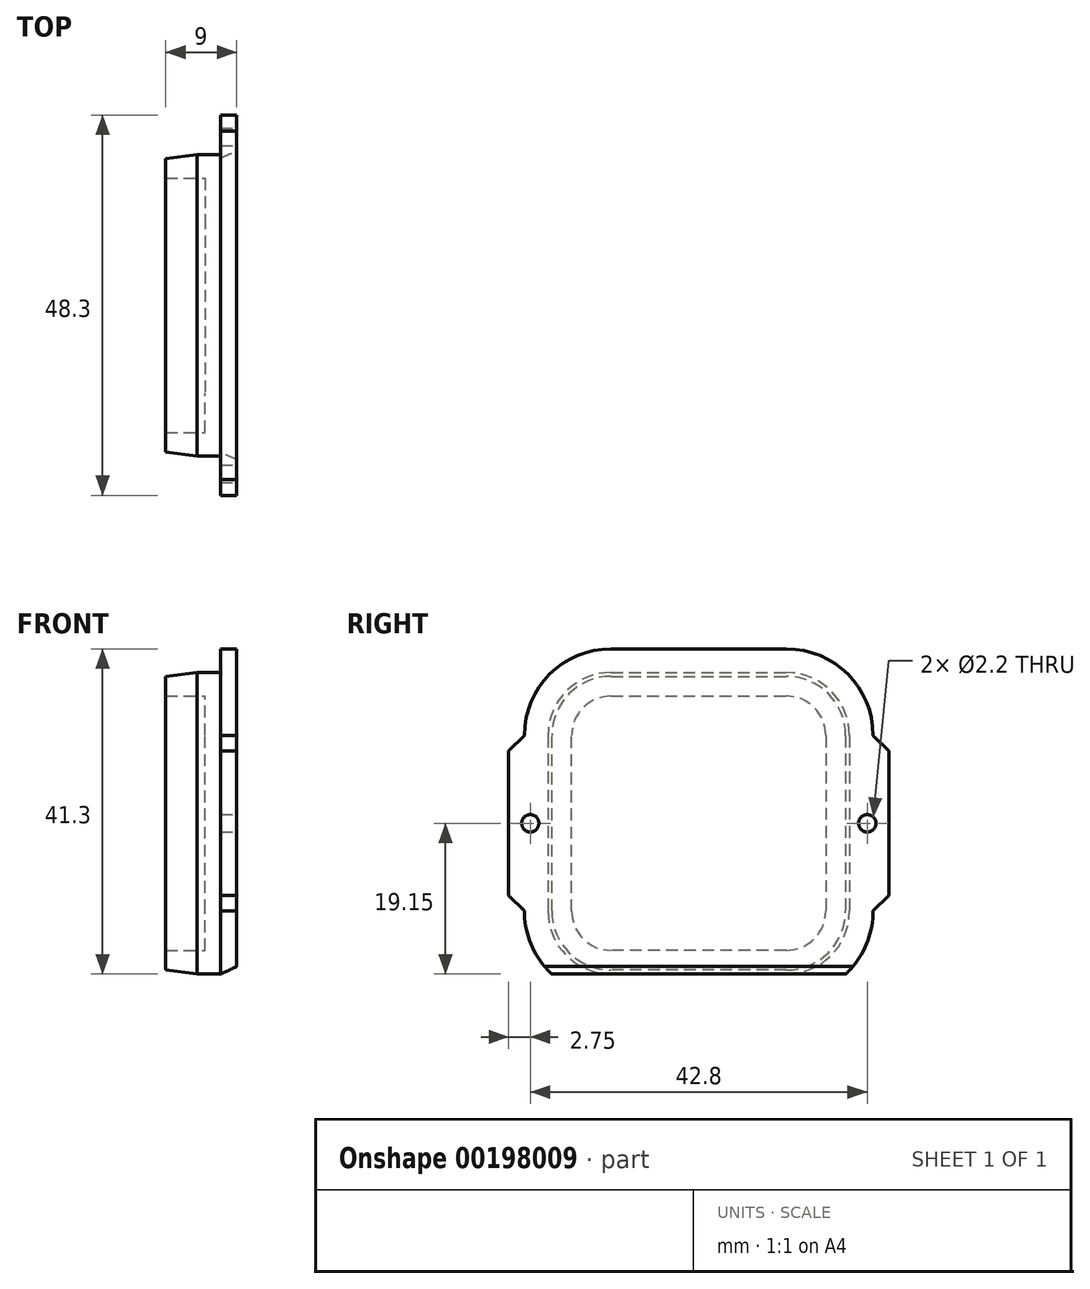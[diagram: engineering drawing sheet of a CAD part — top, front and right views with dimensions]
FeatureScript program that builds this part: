
annotation { "Feature Type Name" : "Feature", "Feature Type Description" : "" }
export const myFeature = defineFeature(function(context is Context, id is Id, definition is map)
    precondition{}
    {
        {
            var Q0;
            Q0=qCreatedBy(makeId("Right.planeOp"),FACE);
            var sketch = newSketch(context, id + "F0", { "sketchPlane" : qUnion([Q0])});
            skLineSegment(sketch, "E0.bottom", {"start": v(-11.15, 18.65) * mm, "end": v(11.15, 18.65) * mm});
            skLineSegment(sketch, "E0.top", {"start": v(-11.15, -19.65) * mm, "end": v(11.15, -19.65) * mm});
            skLineSegment(sketch, "E0.left", {"start": v(-19.15, 10.65) * mm, "end": v(-19.15, -11.65) * mm});
            skLineSegment(sketch, "E0.right", {"start": v(19.15, 10.65) * mm, "end": v(19.15, -11.65) * mm});
            skPoint(sketch, "E1.visualSharp", {"position": v(-19.15, 18.65) * mm});
            skArc(sketch, "E1.filletArc", {"start": v(-11.15, 18.65) * mm, "mid": v(-16.8, 16.3) * mm, "end": v(-19.15, 10.65) * mm});
            skPoint(sketch, "E2.visualSharp", {"position": v(19.15, 18.65) * mm});
            skArc(sketch, "E2.filletArc", {"start": v(19.15, 10.65) * mm, "mid": v(16.8, 16.3) * mm, "end": v(11.15, 18.65) * mm});
            skPoint(sketch, "E3.visualSharp", {"position": v(19.15, -19.65) * mm});
            skArc(sketch, "E3.filletArc", {"start": v(11.15, -19.65) * mm, "mid": v(16.8, -17.3) * mm, "end": v(19.15, -11.65) * mm});
            skPoint(sketch, "E4.visualSharp", {"position": v(-19.15, -19.65) * mm});
            skArc(sketch, "E4.filletArc", {"start": v(-19.15, -11.65) * mm, "mid": v(-16.8, -17.3) * mm, "end": v(-11.15, -19.65) * mm});
            skArc(sketch, "E5.0", {"start": v(-11.15, 21.65) * mm, "mid": v(-18.93, 18.43) * mm, "end": v(-22.15, 10.65) * mm});
            skLineSegment(sketch, "E5.1", {"start": v(-22.15, 10.65) * mm, "end": v(-22.15, -11.65) * mm});
            skLineSegment(sketch, "E5.2", {"start": v(-11.15, 21.65) * mm, "end": v(11.15, 21.65) * mm});
            skArc(sketch, "E5.3", {"start": v(-22.15, -11.65) * mm, "mid": v(-18.93, -19.43) * mm, "end": v(-11.15, -22.65) * mm});
            skArc(sketch, "E5.4", {"start": v(22.15, 10.65) * mm, "mid": v(18.93, 18.43) * mm, "end": v(11.15, 21.65) * mm});
            skLineSegment(sketch, "E5.5", {"start": v(22.15, 10.65) * mm, "end": v(22.15, -11.65) * mm});
            skArc(sketch, "E5.6", {"start": v(11.15, -22.65) * mm, "mid": v(18.93, -19.43) * mm, "end": v(22.15, -11.65) * mm});
            skLineSegment(sketch, "E5.7", {"start": v(-11.15, -22.65) * mm, "end": v(11.15, -22.65) * mm});
            skLineSegment(sketch, "E6", {"start": v(-24.15, -9.65) * mm, "end": v(-24.15, 8.65) * mm});
            skLineSegment(sketch, "E7", {"start": v(-24.15, 8.65) * mm, "end": v(-22.15, 10.65) * mm});
            skLineSegment(sketch, "E8", {"start": v(-22.15, -11.65) * mm, "end": v(-24.15, -9.65) * mm});
            skLineSegment(sketch, "E9.MirrorCS", {"start": v(24.15, 8.65) * mm, "end": v(22.15, 10.65) * mm});
            skLineSegment(sketch, "E10.MirrorCS", {"start": v(24.15, -9.65) * mm, "end": v(24.15, 8.65) * mm});
            skLineSegment(sketch, "E11.MirrorCS", {"start": v(22.15, -11.65) * mm, "end": v(24.15, -9.65) * mm});
            skLineSegment(sketch, "E12", {"start": v(-19.15, -0.5) * mm, "end": v(19.15, -0.5) * mm, "construction": true});
            skLineSegment(sketch, "E13", {"start": v(0, 18.65) * mm, "end": v(0, -19.65) * mm, "construction": true});
            skPoint(sketch, "E14.visualSharp", {"position": v(-16.65, 16.65) * mm});
            skPoint(sketch, "E15", {"position": v(-21.4, -0.5) * mm});
            skPoint(sketch, "E16", {"position": v(-22.15, -0.5) * mm});
            skPoint(sketch, "E17.MirrorP", {"position": v(21.4, -0.5) * mm});
            skSolve(sketch);
        }
        {
            var Q0;
            Q0=makeQuery(id+"F0.imprint","IMPRINT",FACE,{"disambiguationData":[TD([[makeQuery(id+"F0.imprint","IMPRINT",EDGE,{"derivedFrom":sQuery(id+"F0.wireOp",EDGE,"E0.bottom")}),-1.0]])]});
            var Q1;
            Q1=makeQuery(id+"F0.imprint","IMPRINT",FACE,{"disambiguationData":[TD([[makeQuery(id+"F0.imprint","IMPRINT",EDGE,{"derivedFrom":sQuery(id+"F0.wireOp",EDGE,"E0.bottom")}),1.0]])]});
            var Q2;
            Q2=makeQuery(id+"F0.imprint","IMPRINT",FACE,{"disambiguationData":[TD([[makeQuery(id+"F0.imprint","IMPRINT",EDGE,{"derivedFrom":sQuery(id+"F0.wireOp",EDGE,"E5.1")}),-1.0]])]});
            var Q3;
            Q3=makeQuery(id+"F0.imprint","IMPRINT",FACE,{"disambiguationData":[TD([[makeQuery(id+"F0.imprint","IMPRINT",EDGE,{"derivedFrom":sQuery(id+"F0.wireOp",EDGE,"E5.5")}),1.0]])]});
            extrude(context, id + "F1", {"entities" : qUnion([Q0, Q1, Q2, Q3]), "oppositeDirection" : true, "depth" : 2 * mm});
        }
        {
            var Q0;
            Q0=makeQuery(id+"F0.imprint","IMPRINT",FACE,{"disambiguationData":[TD([[makeQuery(id+"F0.imprint","IMPRINT",EDGE,{"derivedFrom":sQuery(id+"F0.wireOp",EDGE,"E0.bottom")}),-1.0]])]});
            extrude(context, id + "F2", {"entities" : qUnion([Q0]), "operationType" : NewBodyOperationType.ADD, "oppositeDirection" : true, "depth" : 4 * mm});
        }
        {
            var Q0;
            Q0=makeQuery(id+"F2.boolean.opBoolean","INTERSECT",EDGE,{"derivedFrom":[makeQuery(id+"F1.opExtrude","CAP_FACE",FACE,{"disambiguationData":[OSD([sQuery(id+"F0.wireOp",EDGE,"E5.0"),sQuery(id+"F0.wireOp",EDGE,"E5.2"),sQuery(id+"F0.wireOp",EDGE,"E5.3"),sQuery(id+"F0.wireOp",EDGE,"E5.4"),sQuery(id+"F0.wireOp",EDGE,"E5.6"),sQuery(id+"F0.wireOp",EDGE,"E5.7"),sQuery(id+"F0.wireOp",EDGE,"E6"),sQuery(id+"F0.wireOp",EDGE,"E7"),sQuery(id+"F0.wireOp",EDGE,"E8"),sQuery(id+"F0.wireOp",EDGE,"E9.MirrorCS"),sQuery(id+"F0.wireOp",EDGE,"E10.MirrorCS"),sQuery(id+"F0.wireOp",EDGE,"E11.MirrorCS"),sQuery(id+"F0.wireOp",EDGE,"RST1X7r3-oKxB-jdrm-FJc1-FZEFyPknjC7n.bottom"),sQuery(id+"F0.wireOp",EDGE,"RST1X7r3-oKxB-jdrm-FJc1-FZEFyPknjC7n.top"),sQuery(id+"F0.wireOp",EDGE,"RST1X7r3-oKxB-jdrm-FJc1-FZEFyPknjC7n.left"),sQuery(id+"F0.wireOp",EDGE,"RST1X7r3-oKxB-jdrm-FJc1-FZEFyPknjC7n.right"),sQuery(id+"F0.wireOp",EDGE,"f47886a1-abc6-43d7-98a8-f8cff71f392d.filletArc"),sQuery(id+"F0.wireOp",EDGE,"5e3ffb94-8ac9-4c8a-9269-9c21b55e64ff.filletArc"),sQuery(id+"F0.wireOp",EDGE,"dd1fbfdf-1fb2-4afd-85d2-cb31fff93166.filletArc"),sQuery(id+"F0.wireOp",EDGE,"E14.filletArc"),sQuery(id+"F0.wireOp",EDGE,"41707f4f-61de-468e-8cde-fad0d991ba2c0.MirrorCS"),sQuery(id+"F0.wireOp",EDGE,"c94bd9be-500d-4d44-b017-d16b26a63a020.MirrorCS"),sQuery(id+"F0.wireOp",EDGE,"8c78eab5-b810-45c1-9855-b0b5e582e1f70.MirrorCS"),sQuery(id+"F0.wireOp",EDGE,"6b2eb93e-fa95-4abc-8643-495f8d23bd850.MirrorCS"),sQuery(id+"F0.wireOp",EDGE,"e98be541-006e-4dad-bcde-d64d35c2e2500.MirrorCS"),sQuery(id+"F0.wireOp",EDGE,"3a2f4d0b-5016-42d9-9411-d42ab24a4ea80.MirrorCS"),sQuery(id+"F0.wireOp",EDGE,"9864ca3c-7186-4b8b-bf48-64fe2223f2a70.MirrorCS"),sQuery(id+"F0.wireOp",EDGE,"28ad38c3-9f67-4266-9024-0f2c2453c1940.MirrorCS"),sQuery(id+"F0.wireOp",EDGE,"bd4dbd89-46a3-4a25-ba81-fe0fc24358690.MirrorCS"),sQuery(id+"F0.wireOp",EDGE,"919fa4dc-a3d8-4998-9de8-7e6e011190fa0.MirrorCS"),sQuery(id+"F0.wireOp",EDGE,"c0e8c9a9-4d36-41b1-b5ef-4927e6b5828c0.MirrorCS"),sQuery(id+"F0.wireOp",EDGE,"65d96819-48be-4bb4-90a4-4548596de35d0.MirrorCS"),sQuery(id+"F0.wireOp",EDGE,"d78f8fef-45e7-4f36-8306-dc5005d627950.MirrorCS"),sQuery(id+"F0.wireOp",EDGE,"cc93ec59-fd94-4fdf-a76b-cf34ac5038500.MirrorCS"),sQuery(id+"F0.wireOp",EDGE,"b5ffeaaf-6a07-455a-ac6d-026a3d01b9ef0.MirrorCS"),sQuery(id+"F0.wireOp",EDGE,"54cb0ba3-91fc-40b9-bd3f-aec4dbbdf1710.MirrorCS"),sQuery(id+"F0.wireOp",EDGE,"ed805bfa-8f41-4e78-a241-45e0847f27010.MirrorCS"),sQuery(id+"F0.wireOp",EDGE,"2de16986-fcdf-4a11-be1b-2661225e98d80.MirrorCS"),sQuery(id+"F0.wireOp",EDGE,"56bdd509-48f3-4dbd-af82-ea80d3fc59200.MirrorCS"),sQuery(id+"F0.wireOp",EDGE,"176b7e12-560a-4aa1-b38f-03d71e9105200.MirrorCS"),sQuery(id+"F0.wireOp",EDGE,"0f632275-472d-4092-9a11-c3f5ca6ce4e90.MirrorCS"),sQuery(id+"F0.wireOp",EDGE,"313d3c47-0811-412c-b21b-6fa3ed4e9cd90.MirrorCS"),sQuery(id+"F0.wireOp",EDGE,"c9272683-ccd8-4751-98f5-67358050bd030.MirrorCS"),sQuery(id+"F0.wireOp",EDGE,"8fdea69b-69b8-45bc-b756-b638989ef7c50.MirrorCS")])],"isStart":false}),makeQuery(id+"F2.opExtrude","SWEPT_FACE",FACE,{"disambiguationData":[OSD([sQuery(id+"F0.wireOp",EDGE,"E0.top")])]})]});
            var Q1;
            {var subQ0=sQuery(id+"F0.wireOp",EDGE,"E14.filletArc");var subQ1=sQuery(id+"F0.wireOp",EDGE,"0f632275-472d-4092-9a11-c3f5ca6ce4e90.MirrorCS");var subQ2=sQuery(id+"F0.wireOp",EDGE,"d78f8fef-45e7-4f36-8306-dc5005d627950.MirrorCS");var subQ3=sQuery(id+"F0.wireOp",EDGE,"e98be541-006e-4dad-bcde-d64d35c2e2500.MirrorCS");Q1=makeQuery(id+"F9bfLVA2CBOZj6R_1.boolean.opBoolean","MERGE",FACE,{"derivedFrom":[makeQuery(id+"F1.opExtrude","CAP_FACE",FACE,{"disambiguationData":[OSD([sQuery(id+"F0.wireOp",EDGE,"E5.0"),sQuery(id+"F0.wireOp",EDGE,"E5.2"),sQuery(id+"F0.wireOp",EDGE,"E5.3"),sQuery(id+"F0.wireOp",EDGE,"E5.4"),sQuery(id+"F0.wireOp",EDGE,"E5.6"),sQuery(id+"F0.wireOp",EDGE,"E5.7"),sQuery(id+"F0.wireOp",EDGE,"E6"),sQuery(id+"F0.wireOp",EDGE,"E7"),sQuery(id+"F0.wireOp",EDGE,"E8"),sQuery(id+"F0.wireOp",EDGE,"E9.MirrorCS"),sQuery(id+"F0.wireOp",EDGE,"E10.MirrorCS"),sQuery(id+"F0.wireOp",EDGE,"E11.MirrorCS"),sQuery(id+"F0.wireOp",EDGE,"RST1X7r3-oKxB-jdrm-FJc1-FZEFyPknjC7n.bottom"),sQuery(id+"F0.wireOp",EDGE,"RST1X7r3-oKxB-jdrm-FJc1-FZEFyPknjC7n.top"),sQuery(id+"F0.wireOp",EDGE,"RST1X7r3-oKxB-jdrm-FJc1-FZEFyPknjC7n.left"),sQuery(id+"F0.wireOp",EDGE,"RST1X7r3-oKxB-jdrm-FJc1-FZEFyPknjC7n.right"),sQuery(id+"F0.wireOp",EDGE,"f47886a1-abc6-43d7-98a8-f8cff71f392d.filletArc"),sQuery(id+"F0.wireOp",EDGE,"5e3ffb94-8ac9-4c8a-9269-9c21b55e64ff.filletArc"),sQuery(id+"F0.wireOp",EDGE,"dd1fbfdf-1fb2-4afd-85d2-cb31fff93166.filletArc"),subQ0,sQuery(id+"F0.wireOp",EDGE,"41707f4f-61de-468e-8cde-fad0d991ba2c0.MirrorCS"),sQuery(id+"F0.wireOp",EDGE,"c94bd9be-500d-4d44-b017-d16b26a63a020.MirrorCS"),sQuery(id+"F0.wireOp",EDGE,"8c78eab5-b810-45c1-9855-b0b5e582e1f70.MirrorCS"),sQuery(id+"F0.wireOp",EDGE,"6b2eb93e-fa95-4abc-8643-495f8d23bd850.MirrorCS"),subQ3,sQuery(id+"F0.wireOp",EDGE,"3a2f4d0b-5016-42d9-9411-d42ab24a4ea80.MirrorCS"),sQuery(id+"F0.wireOp",EDGE,"9864ca3c-7186-4b8b-bf48-64fe2223f2a70.MirrorCS"),sQuery(id+"F0.wireOp",EDGE,"28ad38c3-9f67-4266-9024-0f2c2453c1940.MirrorCS"),sQuery(id+"F0.wireOp",EDGE,"bd4dbd89-46a3-4a25-ba81-fe0fc24358690.MirrorCS"),sQuery(id+"F0.wireOp",EDGE,"919fa4dc-a3d8-4998-9de8-7e6e011190fa0.MirrorCS"),sQuery(id+"F0.wireOp",EDGE,"c0e8c9a9-4d36-41b1-b5ef-4927e6b5828c0.MirrorCS"),sQuery(id+"F0.wireOp",EDGE,"65d96819-48be-4bb4-90a4-4548596de35d0.MirrorCS"),subQ2,sQuery(id+"F0.wireOp",EDGE,"cc93ec59-fd94-4fdf-a76b-cf34ac5038500.MirrorCS"),sQuery(id+"F0.wireOp",EDGE,"b5ffeaaf-6a07-455a-ac6d-026a3d01b9ef0.MirrorCS"),sQuery(id+"F0.wireOp",EDGE,"54cb0ba3-91fc-40b9-bd3f-aec4dbbdf1710.MirrorCS"),sQuery(id+"F0.wireOp",EDGE,"ed805bfa-8f41-4e78-a241-45e0847f27010.MirrorCS"),sQuery(id+"F0.wireOp",EDGE,"2de16986-fcdf-4a11-be1b-2661225e98d80.MirrorCS"),sQuery(id+"F0.wireOp",EDGE,"56bdd509-48f3-4dbd-af82-ea80d3fc59200.MirrorCS"),sQuery(id+"F0.wireOp",EDGE,"176b7e12-560a-4aa1-b38f-03d71e9105200.MirrorCS"),subQ1,sQuery(id+"F0.wireOp",EDGE,"313d3c47-0811-412c-b21b-6fa3ed4e9cd90.MirrorCS"),sQuery(id+"F0.wireOp",EDGE,"c9272683-ccd8-4751-98f5-67358050bd030.MirrorCS"),sQuery(id+"F0.wireOp",EDGE,"8fdea69b-69b8-45bc-b756-b638989ef7c50.MirrorCS")])],"isStart":false}),makeQuery(id+"F9bfLVA2CBOZj6R_1.opExtrude","CAP_FACE",FACE,{"disambiguationData":[OSD([sQuery(id+"F0.wireOp",EDGE,"E2.filletArc"),subQ3,sQuery(id+"Fyzcnke55fN6EYS_1.wireOp",EDGE,"QiR1MtRN-fdwX-WXy4-x771-8BzALy9n0cS3"),sQuery(id+"Fyzcnke55fN6EYS_1.wireOp",EDGE,"vY3vD9Ej-vjfs-RaEq-R8OK-G315fCNPvZiC")])],"isStart":false}),makeQuery(id+"F9bfLVA2CBOZj6R_1.opExtrude","CAP_FACE",FACE,{"disambiguationData":[OSD([sQuery(id+"F0.wireOp",EDGE,"E3.filletArc"),subQ2,sQuery(id+"Fyzcnke55fN6EYS_1.wireOp",EDGE,"HcA47B32-zAgk-f9lA-RzsO-5v7idsMHrOcg"),sQuery(id+"Fyzcnke55fN6EYS_1.wireOp",EDGE,"QsuIJIUJ-5H4d-Hi8I-3jHc-Jza0oheNNiUD")])],"isStart":false}),makeQuery(id+"F9bfLVA2CBOZj6R_1.opExtrude","CAP_FACE",FACE,{"disambiguationData":[OSD([sQuery(id+"F0.wireOp",EDGE,"E4.filletArc"),subQ1,sQuery(id+"Fyzcnke55fN6EYS_1.wireOp",EDGE,"7cDfTqYS-uIh8-kYWj-oEK8-Cs800mwhrqOz"),sQuery(id+"Fyzcnke55fN6EYS_1.wireOp",EDGE,"ZtBWqctN-wIv8-skdU-IZqf-vyyk3XKw92PI")])],"isStart":false}),makeQuery(id+"F9bfLVA2CBOZj6R_1.opExtrude","CAP_FACE",FACE,{"disambiguationData":[OSD([sQuery(id+"F0.wireOp",EDGE,"E1.filletArc"),subQ0,sQuery(id+"Fyzcnke55fN6EYS_1.wireOp",EDGE,"1VuTEMU4-RqXQ-3Vaf-u5Zg-6FnOBHOrzMkE"),sQuery(id+"Fyzcnke55fN6EYS_1.wireOp",EDGE,"HgNnJnaG-CRBc-Oqg8-Lyg3-c9rGoYTjLlFq")])],"isStart":false})]});}
            cPlane(context, id + "F3", {"entities" : qUnion([Q0, Q1]), "cplaneType" : CPlaneType.LINE_ANGLE, "offset" : 25 * mm, "angle" : 65 * degree, "width" : 150 * mm, "height" : 150 * mm});
        }
        {
            var Q0;
            Q0=qCreatedBy(id+"F3.planeOp",FACE);
            var sketch = newSketch(context, id + "F4", { "sketchPlane" : qUnion([Q0])});
            skLineSegment(sketch, "E18.bottom", {"start": v(-20.45, 27.18) * mm, "end": v(3.1, 27.18) * mm});
            skLineSegment(sketch, "E18.top", {"start": v(-20.45, -36.35) * mm, "end": v(3.1, -36.35) * mm});
            skLineSegment(sketch, "E18.left", {"start": v(-20.45, 27.18) * mm, "end": v(-20.45, -36.35) * mm});
            skLineSegment(sketch, "E18.right", {"start": v(3.1, 27.18) * mm, "end": v(3.1, -36.35) * mm});
            skSolve(sketch);
        }
        {
            var Q0;
            Q0=makeQuery(id+"F4.imprint","IMPRINT",FACE,{"disambiguationData":[TD([[makeQuery(id+"F4.imprint","IMPRINT",EDGE,{"derivedFrom":sQuery(id+"F4.wireOp",EDGE,"E18.bottom")}),-1.0]])]});
            extrude(context, id + "F5", {"entities" : qUnion([Q0]), "operationType" : NewBodyOperationType.REMOVE, "endBound" : BoundingType.THROUGH_ALL, "depth" : 25 * mm});
        }
        {
            var Q0;
            Q0=makeQuery(id+"F2.opExtrude","CAP_FACE",FACE,{"disambiguationData":[OSD([sQuery(id+"F0.wireOp",EDGE,"E0.bottom"),sQuery(id+"F0.wireOp",EDGE,"E0.top"),sQuery(id+"F0.wireOp",EDGE,"E0.left"),sQuery(id+"F0.wireOp",EDGE,"E0.right"),sQuery(id+"F0.wireOp",EDGE,"E1.filletArc"),sQuery(id+"F0.wireOp",EDGE,"E2.filletArc"),sQuery(id+"F0.wireOp",EDGE,"E3.filletArc"),sQuery(id+"F0.wireOp",EDGE,"E4.filletArc")])],"isStart":false});
            var sketch = newSketch(context, id + "F6", { "sketchPlane" : qUnion([Q0])});
            skArc(sketch, "E19.0", {"start": v(16.15, 10.65) * mm, "mid": v(14.69, 14.19) * mm, "end": v(11.15, 15.65) * mm});
            skLineSegment(sketch, "E19.1", {"start": v(16.15, -11.65) * mm, "end": v(16.15, 10.65) * mm});
            skLineSegment(sketch, "E19.2", {"start": v(11.15, 15.65) * mm, "end": v(-11.15, 15.65) * mm});
            skArc(sketch, "E19.3", {"start": v(11.15, -16.65) * mm, "mid": v(14.69, -15.19) * mm, "end": v(16.15, -11.65) * mm});
            skArc(sketch, "E19.4", {"start": v(-11.15, 15.65) * mm, "mid": v(-14.69, 14.19) * mm, "end": v(-16.15, 10.65) * mm});
            skLineSegment(sketch, "E19.5", {"start": v(-16.15, 10.65) * mm, "end": v(-16.15, -11.65) * mm});
            skArc(sketch, "E19.6", {"start": v(-16.15, -11.65) * mm, "mid": v(-14.69, -15.19) * mm, "end": v(-11.15, -16.65) * mm});
            skLineSegment(sketch, "E19.7", {"start": v(-11.15, -16.65) * mm, "end": v(11.15, -16.65) * mm});
            skSolve(sketch);
        }
        {
            var Q0;
            Q0=makeQuery(id+"F6.imprint","IMPRINT",FACE,{"disambiguationData":[TD([[makeQuery(id+"F6.imprint","IMPRINT",EDGE,{"derivedFrom":sQuery(id+"F6.wireOp",EDGE,"E19.0")}),-1.0]])]});
            extrude(context, id + "F7", {"entities" : qUnion([Q0]), "operationType" : NewBodyOperationType.ADD, "depth" : 5 * mm});
        }
        {
            var Q0;
            Q0=makeQuery(id+"F7.opExtrude","CAP_EDGE",EDGE,{"disambiguationData":[OSD([sQuery(id+"F0.wireOp",EDGE,"E4.filletArc")])],"isStart":false});
            var Q1;
            Q1=makeQuery(id+"F7.opExtrude","CAP_EDGE",EDGE,{"disambiguationData":[OSD([sQuery(id+"F0.wireOp",EDGE,"E0.top")])],"isStart":false});
            var Q2;
            Q2=makeQuery(id+"F7.opExtrude","CAP_EDGE",EDGE,{"disambiguationData":[OSD([sQuery(id+"F0.wireOp",EDGE,"E0.left")])],"isStart":false});
            chamfer(context, id + "F8", {"entities" : qUnion([Q0, Q1, Q2]), "chamferType" : ChamferType.TWO_OFFSETS, "width1" : 4 * mm, "oppositeDirection" : false, "width2" : 0.5 * mm, "tangentPropagation" : true});
        }
        {
            var Q0;
            Q0=sQuery(id+"F0.wireOp",VERTEX,"E15");
            var Q1;
            Q1=sQuery(id+"F0.wireOp",VERTEX,"E17.MirrorP");
            var Q2;
            Q2=makeQuery(id+"F1.opExtrude","SWEPT_BODY",BODY,{"disambiguationData":[OSD([sQuery(id+"F0.wireOp",EDGE,"E5.0"),sQuery(id+"F0.wireOp",EDGE,"E5.2"),sQuery(id+"F0.wireOp",EDGE,"E5.3"),sQuery(id+"F0.wireOp",EDGE,"E5.4"),sQuery(id+"F0.wireOp",EDGE,"E5.6"),sQuery(id+"F0.wireOp",EDGE,"E5.7"),sQuery(id+"F0.wireOp",EDGE,"E6"),sQuery(id+"F0.wireOp",EDGE,"E7"),sQuery(id+"F0.wireOp",EDGE,"E8"),sQuery(id+"F0.wireOp",EDGE,"E9.MirrorCS"),sQuery(id+"F0.wireOp",EDGE,"E10.MirrorCS"),sQuery(id+"F0.wireOp",EDGE,"E11.MirrorCS")])]});
            hole(context, id + "F9", {"style" : HoleStyle.SIMPLE, "endStyle" : HoleEndStyle.THROUGH, "holeDiameter" : 2.2 * mm, "locations" : qUnion([Q0, Q1]), "scope" : qUnion([Q2]), "isTappedThrough" : true});
        }
    });
